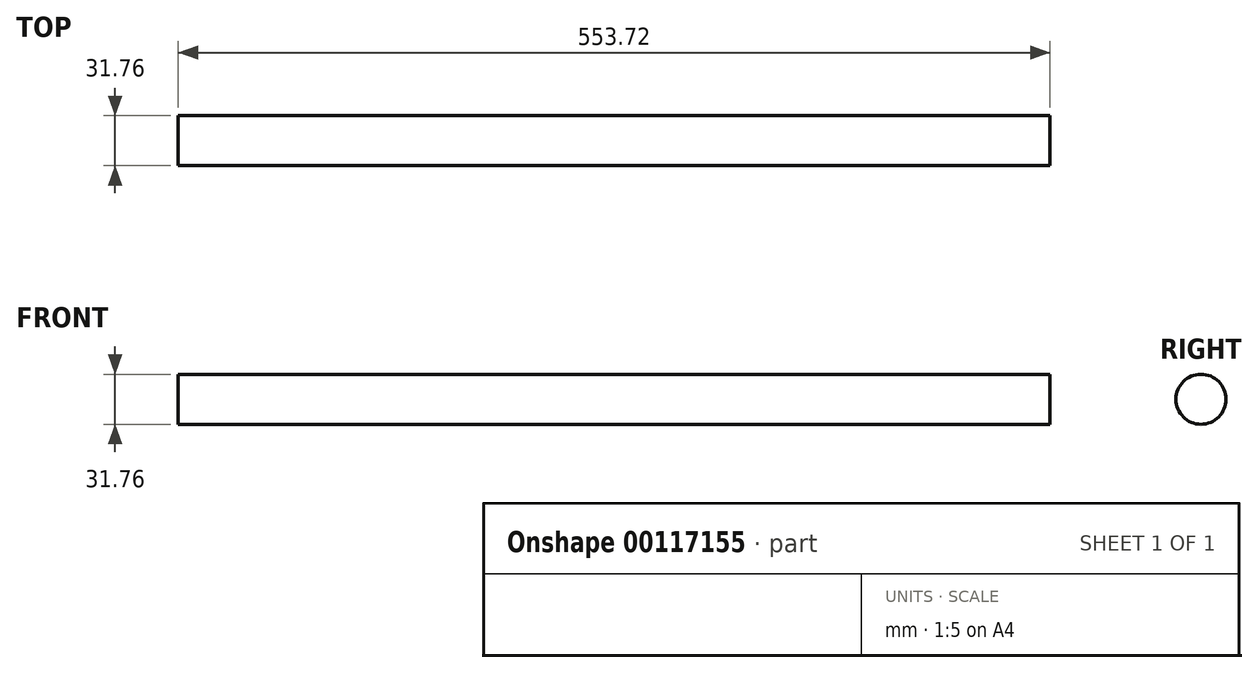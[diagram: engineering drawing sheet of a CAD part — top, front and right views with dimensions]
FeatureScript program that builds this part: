
annotation { "Feature Type Name" : "Feature", "Feature Type Description" : "" }
export const myFeature = defineFeature(function(context is Context, id is Id, definition is map)
    precondition{}
    {
        {
            var Q0;
            Q0=qCreatedBy(makeId("Front.planeOp"),FACE);
            var sketch = newSketch(context, id + "F0", { "sketchPlane" : qUnion([Q0])});
            skLineSegment(sketch, "E0", {"start": v(0, 0) * mm, "end": v(0, 15.88) * mm});
            skLineSegment(sketch, "E1", {"start": v(0, 15.88) * mm, "end": v(-553.72, 15.88) * mm});
            skLineSegment(sketch, "E2", {"start": v(-553.72, 15.88) * mm, "end": v(-553.72, 0) * mm});
            skLineSegment(sketch, "E3", {"start": v(-553.72, 0) * mm, "end": v(0, 0) * mm});
            skSolve(sketch);
        }
        {
            var Q0;
            Q0=makeQuery(id+"F0.imprint","IMPRINT",FACE,{"disambiguationData":[TD([[makeQuery(id+"F0.imprint","IMPRINT",EDGE,{"derivedFrom":sQuery(id+"F0.wireOp",EDGE,"E0")}),1.0]])]});
            var Q1;
            Q1=sQuery(id+"F0.wireOp",EDGE,"E3");
            revolve(context, id + "F1", {"entities" : qUnion([Q0]), "axis" : qUnion([Q1]), "revolveType" : RevolveType.FULL});
        }
    });
